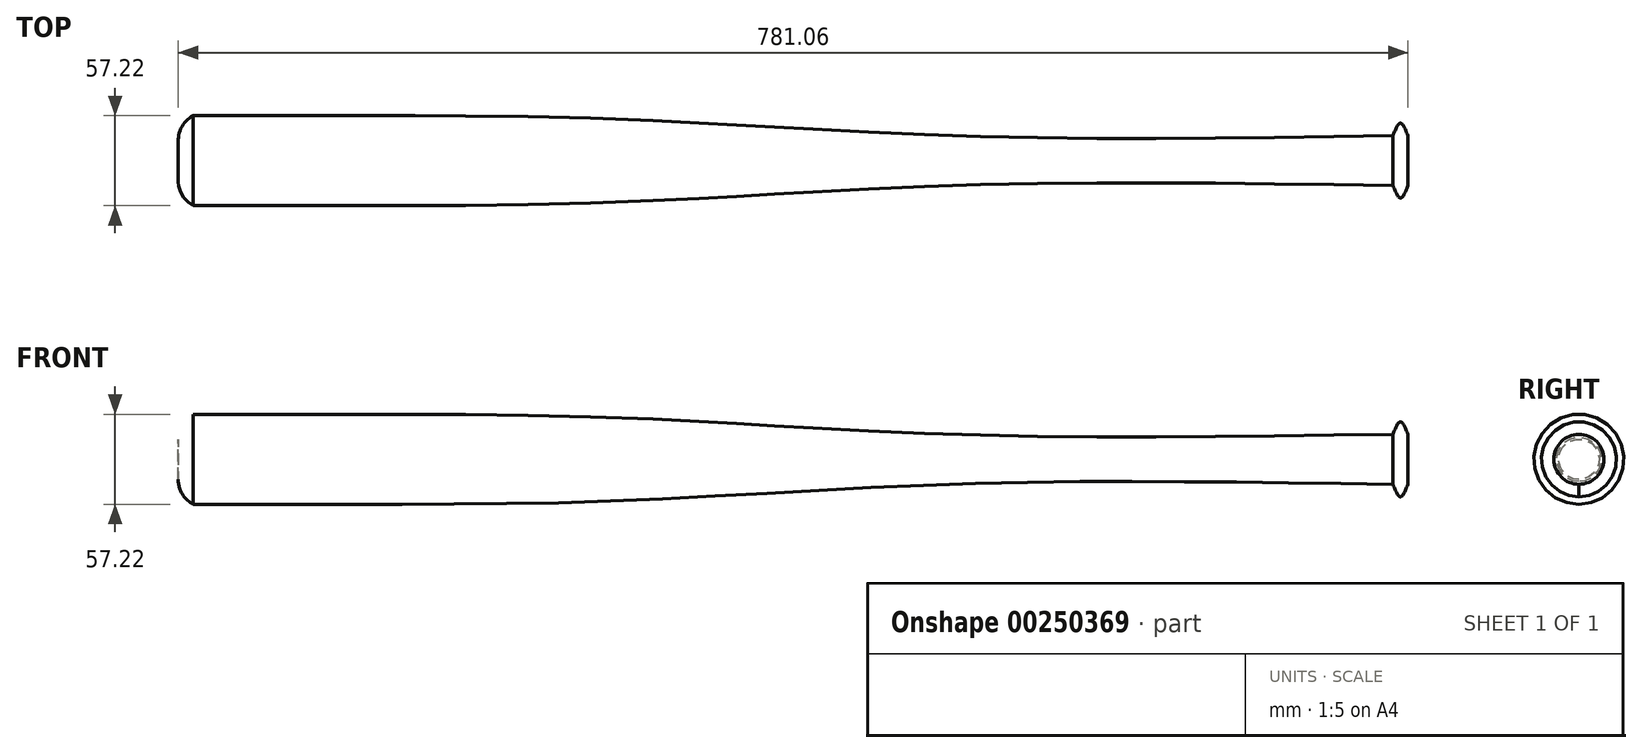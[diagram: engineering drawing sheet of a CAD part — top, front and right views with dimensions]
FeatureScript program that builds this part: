
annotation { "Feature Type Name" : "Feature", "Feature Type Description" : "" }
export const myFeature = defineFeature(function(context is Context, id is Id, definition is map)
    precondition{}
    {
        {
            var Q0;
            Q0=qCreatedBy(makeId("Right.planeOp"),FACE);
            cPlane(context, id + "F0", {"entities" : qUnion([Q0]), "cplaneType" : CPlaneType.OFFSET, "offset" : 4.76 * mm, "width" : 152.4 * mm, "height" : 152.4 * mm});
        }
        {
            var Q0;
            Q0=qCreatedBy(makeId("Right.planeOp"),FACE);
            var sketch = newSketch(context, id + "F1", { "sketchPlane" : qUnion([Q0])});
            skCircle(sketch, "E0", {"center": v(0, 0) * mm, "radius": 15.88 * mm});
            skSolve(sketch);
        }
        {
            var Q0;
            Q0=qCreatedBy(id+"F0.planeOp",FACE);
            var sketch = newSketch(context, id + "F2", { "sketchPlane" : qUnion([Q0])});
            skCircle(sketch, "E1", {"center": v(0, 0) * mm, "radius": 23.81 * mm});
            skSolve(sketch);
        }
        {
            var Q0;
            Q0=qCreatedBy(makeId("Right.planeOp"),FACE);
            cPlane(context, id + "F3", {"entities" : qUnion([Q0]), "cplaneType" : CPlaneType.OFFSET, "offset" : 127 * mm, "oppositeDirection" : true, "width" : 152.4 * mm, "height" : 152.4 * mm});
        }
        {
            var Q0;
            Q0=qCreatedBy(id+"F3.planeOp",FACE);
            var sketch = newSketch(context, id + "F4", { "sketchPlane" : qUnion([Q0])});
            skCircle(sketch, "E2", {"center": v(0, 0) * mm, "radius": 14.29 * mm});
            skSolve(sketch);
        }
        {
            var Q0;
            Q0=qCreatedBy(id+"F3.planeOp",FACE);
            cPlane(context, id + "F5", {"entities" : qUnion([Q0]), "cplaneType" : CPlaneType.OFFSET, "offset" : 127 * mm, "oppositeDirection" : true, "width" : 152.4 * mm, "height" : 152.4 * mm});
        }
        {
            var Q0;
            Q0=qCreatedBy(id+"F5.planeOp",FACE);
            var sketch = newSketch(context, id + "F6", { "sketchPlane" : qUnion([Q0])});
            skCircle(sketch, "E3", {"center": v(0, 0) * mm, "radius": 15.08 * mm});
            skSolve(sketch);
        }
        {
            var Q0;
            Q0=qCreatedBy(id+"F5.planeOp",FACE);
            cPlane(context, id + "F7", {"entities" : qUnion([Q0]), "cplaneType" : CPlaneType.OFFSET, "offset" : 127 * mm, "oppositeDirection" : true, "width" : 152.4 * mm, "height" : 152.4 * mm});
        }
        {
            var Q0;
            Q0=qCreatedBy(id+"F7.planeOp",FACE);
            var sketch = newSketch(context, id + "F8", { "sketchPlane" : qUnion([Q0])});
            skCircle(sketch, "E4", {"center": v(0, 0) * mm, "radius": 20.64 * mm});
            skSolve(sketch);
        }
        {
            var Q0;
            Q0=qCreatedBy(id+"F7.planeOp",FACE);
            cPlane(context, id + "F9", {"entities" : qUnion([Q0]), "cplaneType" : CPlaneType.OFFSET, "offset" : 127 * mm, "oppositeDirection" : true, "width" : 152.4 * mm, "height" : 152.4 * mm});
        }
        {
            var Q0;
            Q0=qCreatedBy(id+"F9.planeOp",FACE);
            var sketch = newSketch(context, id + "F10", { "sketchPlane" : qUnion([Q0])});
            skCircle(sketch, "E5", {"center": v(0, 0) * mm, "radius": 26.99 * mm});
            skSolve(sketch);
        }
        {
            var Q0;
            Q0=qCreatedBy(id+"F9.planeOp",FACE);
            cPlane(context, id + "F11", {"entities" : qUnion([Q0]), "cplaneType" : CPlaneType.OFFSET, "offset" : 127 * mm, "oppositeDirection" : true, "width" : 152.4 * mm, "height" : 152.4 * mm});
        }
        {
            var Q0;
            Q0=qCreatedBy(id+"F11.planeOp",FACE);
            var sketch = newSketch(context, id + "F12", { "sketchPlane" : qUnion([Q0])});
            skCircle(sketch, "E6", {"center": v(0, 0) * mm, "radius": 28.58 * mm});
            skSolve(sketch);
        }
        {
            var Q0;
            Q0=qCreatedBy(id+"F11.planeOp",FACE);
            cPlane(context, id + "F13", {"entities" : qUnion([Q0]), "cplaneType" : CPlaneType.OFFSET, "offset" : 127 * mm, "oppositeDirection" : true, "width" : 152.4 * mm, "height" : 152.4 * mm});
        }
        {
            var Q0;
            Q0=qCreatedBy(id+"F13.planeOp",FACE);
            var sketch = newSketch(context, id + "F14", { "sketchPlane" : qUnion([Q0])});
            skCircle(sketch, "E7", {"center": v(0, 0) * mm, "radius": 28.58 * mm});
            skSolve(sketch);
        }
        {
            var Q0;
            Q0=qCreatedBy(id+"F13.planeOp",FACE);
            cPlane(context, id + "F15", {"entities" : qUnion([Q0]), "cplaneType" : CPlaneType.OFFSET, "offset" : 9.52 * mm, "oppositeDirection" : true, "width" : 152.4 * mm, "height" : 152.4 * mm});
        }
        {
            var Q0;
            Q0=qCreatedBy(id+"F15.planeOp",FACE);
            var sketch = newSketch(context, id + "F16", { "sketchPlane" : qUnion([Q0])});
            skCircle(sketch, "E8", {"center": v(0, 0) * mm, "radius": 23.81 * mm});
            skSolve(sketch);
        }
        {
            var Q0;
            Q0=qCreatedBy(id+"F0.planeOp",FACE);
            cPlane(context, id + "F17", {"entities" : qUnion([Q0]), "cplaneType" : CPlaneType.OFFSET, "offset" : 4.76 * mm, "width" : 152.4 * mm, "height" : 152.4 * mm});
        }
        {
            var Q0;
            Q0=qCreatedBy(id+"F17.planeOp",FACE);
            var sketch = newSketch(context, id + "F18", { "sketchPlane" : qUnion([Q0])});
            skCircle(sketch, "E9", {"center": v(0, 0) * mm, "radius": 15.88 * mm});
            skSolve(sketch);
        }
        {
            var Q0;
            Q0=makeQuery(id+"F16.imprint","IMPRINT",FACE,{"disambiguationData":[TD([[makeQuery(id+"F16.imprint","IMPRINT",EDGE,{"derivedFrom":sQuery(id+"F16.wireOp",EDGE,"E8")}),1.0]])]});
            var Q1;
            Q1=makeQuery(id+"F14.imprint","IMPRINT",FACE,{"disambiguationData":[TD([[makeQuery(id+"F14.imprint","IMPRINT",EDGE,{"derivedFrom":sQuery(id+"F14.wireOp",EDGE,"E7")}),1.0]])]});
            loft(context, id + "F19", {"sheetProfilesArray" : [{ "sheetProfileEntities" : qUnion([Q0]) }, { "sheetProfileEntities" : qUnion([Q1]) }]});
        }
        {
            var Q0;
            Q0=makeQuery(id+"F19.opLoft","CAP_FACE",FACE,{"disambiguationData":[OSD([makeQuery(id+"F14.imprint","IMPRINT",FACE,{"disambiguationData":[TD([[makeQuery(id+"F14.imprint","IMPRINT",EDGE,{"derivedFrom":sQuery(id+"F14.wireOp",EDGE,"E7")}),1.0]])]})])],"isStart":true});
            var Q1;
            Q1=makeQuery(id+"F12.imprint","IMPRINT",FACE,{"disambiguationData":[TD([[makeQuery(id+"F12.imprint","IMPRINT",EDGE,{"derivedFrom":sQuery(id+"F12.wireOp",EDGE,"E6")}),1.0]])]});
            var Q2;
            Q2=makeQuery(id+"F10.imprint","IMPRINT",FACE,{"disambiguationData":[TD([[makeQuery(id+"F10.imprint","IMPRINT",EDGE,{"derivedFrom":sQuery(id+"F10.wireOp",EDGE,"E5")}),1.0]])]});
            var Q3;
            Q3=makeQuery(id+"F8.imprint","IMPRINT",FACE,{"disambiguationData":[TD([[makeQuery(id+"F8.imprint","IMPRINT",EDGE,{"derivedFrom":sQuery(id+"F8.wireOp",EDGE,"E4")}),1.0]])]});
            var Q4;
            Q4=makeQuery(id+"F6.imprint","IMPRINT",FACE,{"disambiguationData":[TD([[makeQuery(id+"F6.imprint","IMPRINT",EDGE,{"derivedFrom":sQuery(id+"F6.wireOp",EDGE,"E3")}),1.0]])]});
            var Q5;
            Q5=makeQuery(id+"F4.imprint","IMPRINT",FACE,{"disambiguationData":[TD([[makeQuery(id+"F4.imprint","IMPRINT",EDGE,{"derivedFrom":sQuery(id+"F4.wireOp",EDGE,"E2")}),1.0]])]});
            var Q6;
            Q6=makeQuery(id+"F1.imprint","IMPRINT",FACE,{"disambiguationData":[TD([[makeQuery(id+"F1.imprint","IMPRINT",EDGE,{"derivedFrom":sQuery(id+"F1.wireOp",EDGE,"E0")}),1.0]])]});
            loft(context, id + "F20", {"operationType" : NewBodyOperationType.ADD, "sheetProfilesArray" : [{ "sheetProfileEntities" : qUnion([Q0]) }, { "sheetProfileEntities" : qUnion([Q1]) }, { "sheetProfileEntities" : qUnion([Q2]) }, { "sheetProfileEntities" : qUnion([Q3]) }, { "sheetProfileEntities" : qUnion([Q4]) }, { "sheetProfileEntities" : qUnion([Q5]) }, { "sheetProfileEntities" : qUnion([Q6]) }]});
        }
        {
            var Q1;
            Q1=makeQuery(id+"F20.opLoft","CAP_FACE",FACE,{"disambiguationData":[OSD([makeQuery(id+"F1.imprint","IMPRINT",FACE,{"disambiguationData":[TD([[makeQuery(id+"F1.imprint","IMPRINT",EDGE,{"derivedFrom":sQuery(id+"F1.wireOp",EDGE,"E0")}),1.0]])]})])],"isStart":true});
            var Q2;
            Q2=makeQuery(id+"F2.imprint","IMPRINT",FACE,{"disambiguationData":[TD([[makeQuery(id+"F2.imprint","IMPRINT",EDGE,{"derivedFrom":sQuery(id+"F2.wireOp",EDGE,"E1")}),1.0]])]});
            var Q3;
            Q3=makeQuery(id+"F18.imprint","IMPRINT",FACE,{"disambiguationData":[TD([[makeQuery(id+"F18.imprint","IMPRINT",EDGE,{"derivedFrom":sQuery(id+"F18.wireOp",EDGE,"E9")}),1.0]])]});
            loft(context, id + "F21", {"operationType" : NewBodyOperationType.ADD, "sheetProfilesArray" : [{ "sheetProfileEntities" : qUnion([Q1]) }, { "sheetProfileEntities" : qUnion([Q2]) }, { "sheetProfileEntities" : qUnion([Q3]) }]});
        }
        {
            var Q0;
            Q0=makeQuery(id+"F19.opLoft","CAP_FACE",FACE,{"disambiguationData":[OSD([makeQuery(id+"F16.imprint","IMPRINT",FACE,{"disambiguationData":[TD([[makeQuery(id+"F16.imprint","IMPRINT",EDGE,{"derivedFrom":sQuery(id+"F16.wireOp",EDGE,"E8")}),1.0]])]})])],"isStart":true});
            fillet(context, id + "F22", {"entities" : qUnion([Q0]), "radius" : 17.78 * mm, "tangentPropagation" : true, "allowEdgeOverflow" : false});
        }
    });
